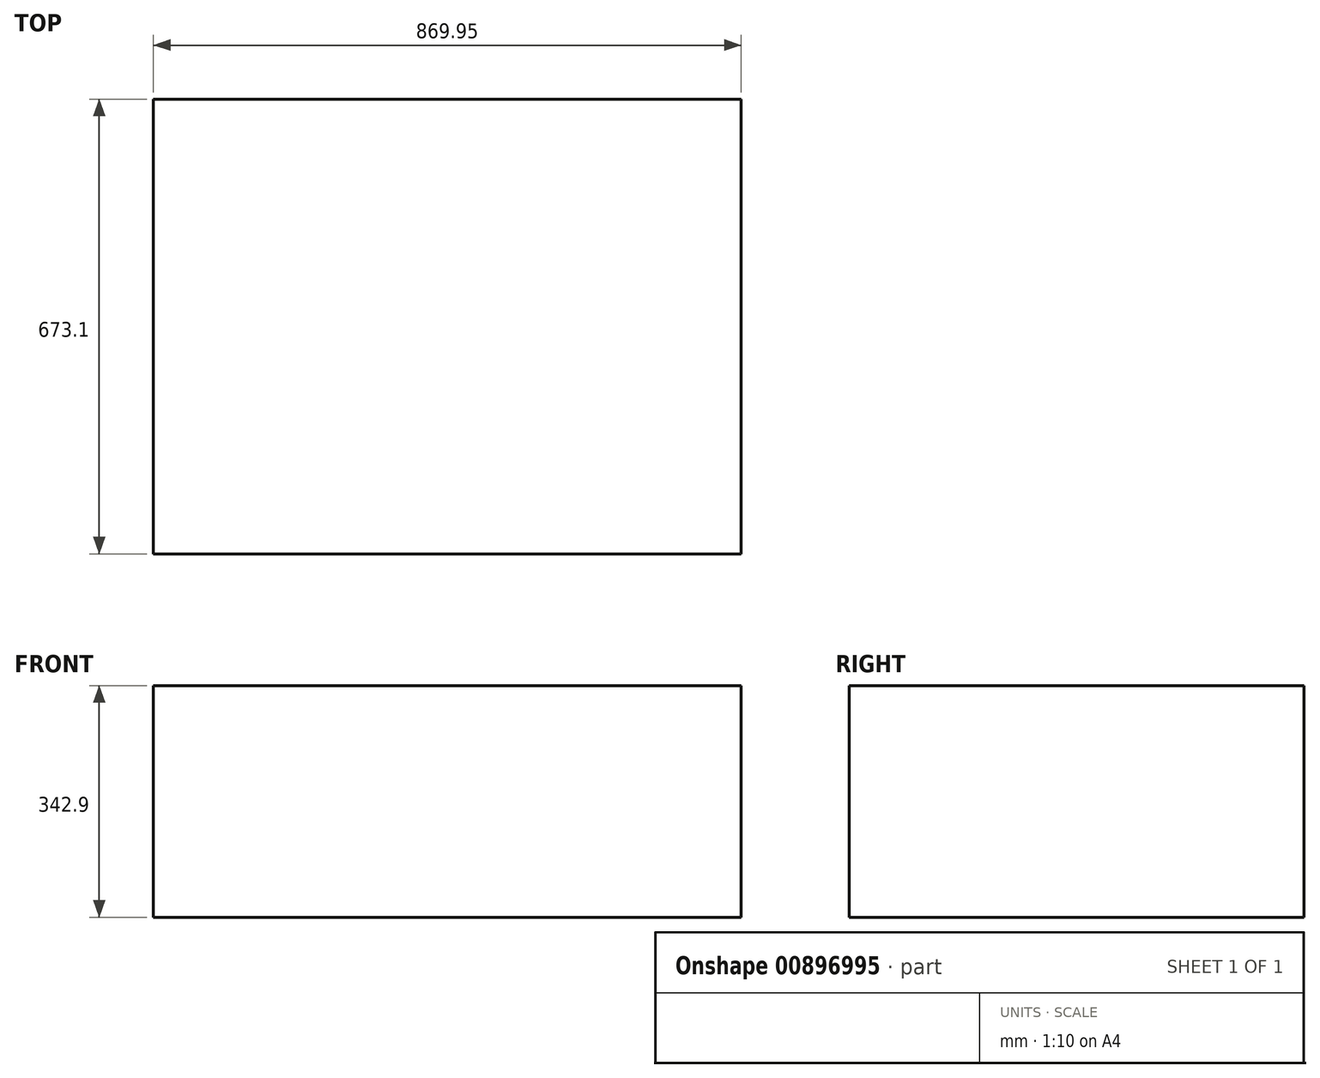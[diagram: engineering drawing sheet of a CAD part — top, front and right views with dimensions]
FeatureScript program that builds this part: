
annotation { "Feature Type Name" : "Feature", "Feature Type Description" : "" }
export const myFeature = defineFeature(function(context is Context, id is Id, definition is map)
    precondition{}
    {
        {
            var Q0;
            Q0=qCreatedBy(makeId("Top.planeOp"),FACE);
            var sketch = newSketch(context, id + "F0", { "sketchPlane" : qUnion([Q0])});
            skLineSegment(sketch, "E0.bottom", {"start": v(0, 0) * mm, "end": v(869.95, 0) * mm});
            skLineSegment(sketch, "E0.top", {"start": v(0, 673.1) * mm, "end": v(869.95, 673.1) * mm});
            skLineSegment(sketch, "E0.left", {"start": v(0, 0) * mm, "end": v(0, 673.1) * mm});
            skLineSegment(sketch, "E0.right", {"start": v(869.95, 0) * mm, "end": v(869.95, 673.1) * mm});
            skSolve(sketch);
        }
        {
            var Q0;
            Q0 = qSketchRegion(id + "F0", true);
            extrude(context, id + "F1", {"entities" : qUnion([Q0]), "depth" : 342.9 * mm, "offsetDistance" : 25.4 * mm});
        }
    });
